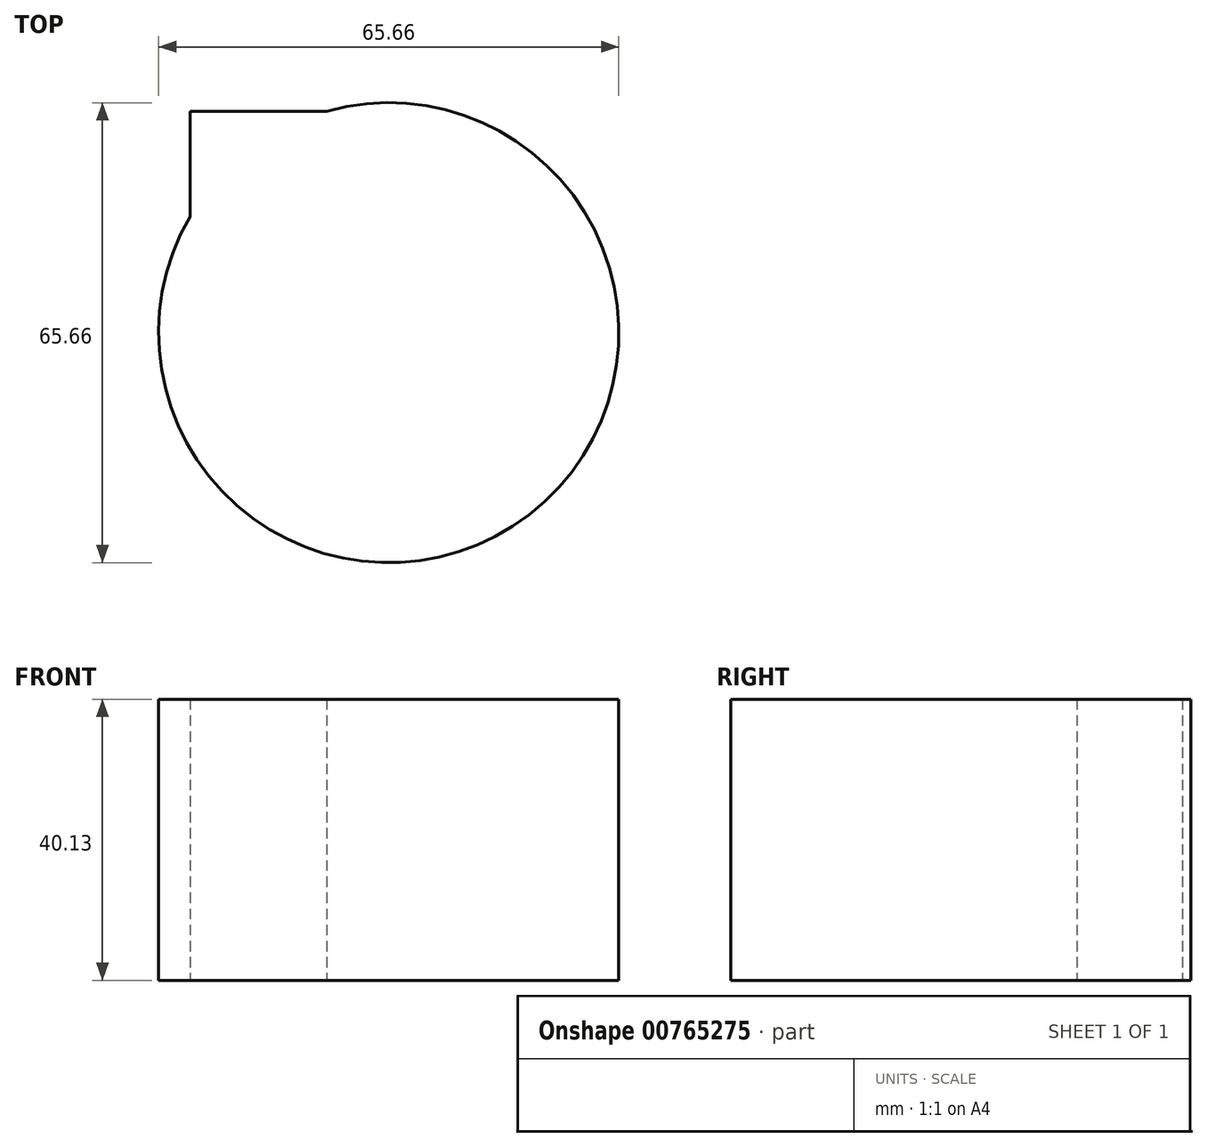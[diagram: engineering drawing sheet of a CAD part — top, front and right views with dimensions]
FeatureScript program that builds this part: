
annotation { "Feature Type Name" : "Feature", "Feature Type Description" : "" }
export const myFeature = defineFeature(function(context is Context, id is Id, definition is map)
    precondition{}
    {
        {
            var Q0;
            Q0=qCreatedBy(makeId("Top.planeOp"),FACE);
            var sketch = newSketch(context, id + "F0", { "sketchPlane" : qUnion([Q0])});
            skCircle(sketch, "E0", {"center": v(0, 0) * mm, "radius": 32.83 * mm});
            skLineSegment(sketch, "E1.bottom", {"start": v(-28.35, 31.63) * mm, "end": v(0, 31.63) * mm});
            skLineSegment(sketch, "E1.top", {"start": v(-28.35, 0) * mm, "end": v(0, 0) * mm});
            skLineSegment(sketch, "E1.left", {"start": v(-28.35, 31.63) * mm, "end": v(-28.35, 0) * mm});
            skLineSegment(sketch, "E1.right", {"start": v(0, 31.63) * mm, "end": v(0, 0) * mm});
            skSolve(sketch);
        }
        {
            var Q0;
            Q0 = qSketchRegion(id + "F0", true);
            extrude(context, id + "F1", {"entities" : qUnion([Q0]), "depth" : 40.13 * mm, "offsetDistance" : 25.4 * mm});
        }
    });
